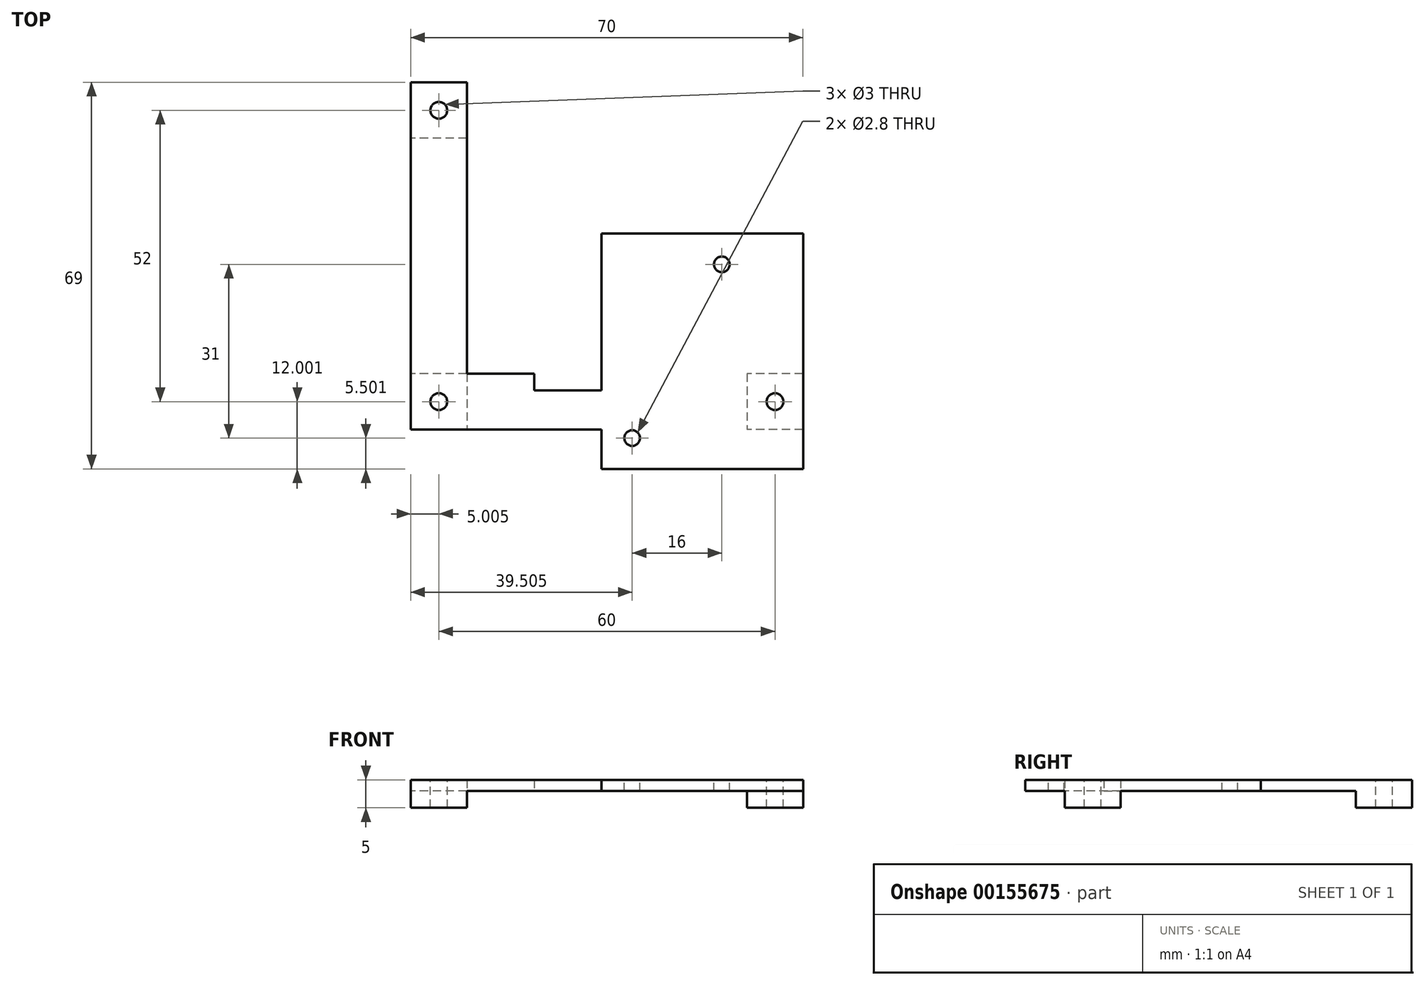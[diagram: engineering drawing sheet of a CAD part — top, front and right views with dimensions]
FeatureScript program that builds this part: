
annotation { "Feature Type Name" : "Feature", "Feature Type Description" : "" }
export const myFeature = defineFeature(function(context is Context, id is Id, definition is map)
    precondition{}
    {
        {
            var Q0;
            Q0=qCreatedBy(makeId("Top.planeOp"),FACE);
            var sketch = newSketch(context, id + "F0", { "sketchPlane" : qUnion([Q0])});
            skLineSegment(sketch, "E0", {"start": v(-62.44, 59.41) * mm, "end": v(-52.44, 59.41) * mm});
            skLineSegment(sketch, "E1", {"start": v(-52.44, 59.41) * mm, "end": v(-52.44, 7.41) * mm});
            skLineSegment(sketch, "E2", {"start": v(-52.44, 7.41) * mm, "end": v(-40.44, 7.41) * mm});
            skLineSegment(sketch, "E3", {"start": v(-40.44, 7.41) * mm, "end": v(-40.44, 4.41) * mm});
            skLineSegment(sketch, "E4", {"start": v(-40.44, 4.41) * mm, "end": v(-28.44, 4.41) * mm});
            skLineSegment(sketch, "E5", {"start": v(-28.44, 4.41) * mm, "end": v(-28.44, 32.41) * mm});
            skLineSegment(sketch, "E6", {"start": v(-28.44, 32.41) * mm, "end": v(7.56, 32.41) * mm});
            skLineSegment(sketch, "E7", {"start": v(7.56, 32.41) * mm, "end": v(7.56, -9.59) * mm});
            skLineSegment(sketch, "E8", {"start": v(7.56, -9.59) * mm, "end": v(-28.44, -9.59) * mm});
            skLineSegment(sketch, "E9", {"start": v(-28.44, -9.59) * mm, "end": v(-28.44, -2.59) * mm});
            skLineSegment(sketch, "E10", {"start": v(-28.44, -2.59) * mm, "end": v(-62.44, -2.59) * mm});
            skLineSegment(sketch, "E11", {"start": v(-62.44, -2.59) * mm, "end": v(-62.44, 59.41) * mm});
            skSolve(sketch);
        }
        {
            var Q0;
            Q0 = qSketchRegion(id + "F0", true);
            extrude(context, id + "F1", {"entities" : qUnion([Q0]), "depth" : 2 * mm});
        }
        {
            var Q0;
            Q0=makeQuery(id+"F1.opExtrude","CAP_FACE",FACE,{"disambiguationData":[OSD([sQuery(id+"F0.wireOp",EDGE,"E0"),sQuery(id+"F0.wireOp",EDGE,"E1"),sQuery(id+"F0.wireOp",EDGE,"E2"),sQuery(id+"F0.wireOp",EDGE,"E3"),sQuery(id+"F0.wireOp",EDGE,"E4"),sQuery(id+"F0.wireOp",EDGE,"E5"),sQuery(id+"F0.wireOp",EDGE,"E6"),sQuery(id+"F0.wireOp",EDGE,"E7"),sQuery(id+"F0.wireOp",EDGE,"E8"),sQuery(id+"F0.wireOp",EDGE,"E9"),sQuery(id+"F0.wireOp",EDGE,"E10"),sQuery(id+"F0.wireOp",EDGE,"E11")])],"isStart":true});
            var sketch = newSketch(context, id + "F2", { "sketchPlane" : qUnion([Q0])});
            skLineSegment(sketch, "E12.bottom", {"start": v(-52.44, -59.41) * mm, "end": v(-62.44, -59.41) * mm});
            skLineSegment(sketch, "E12.top", {"start": v(-52.44, -49.41) * mm, "end": v(-62.44, -49.41) * mm});
            skLineSegment(sketch, "E12.left", {"start": v(-52.44, -59.41) * mm, "end": v(-52.44, -49.41) * mm});
            skLineSegment(sketch, "E12.right", {"start": v(-62.44, -59.41) * mm, "end": v(-62.44, -49.41) * mm});
            skPoint(sketch, "E12.middle", {"position": v(-57.44, -54.41) * mm});
            skLineSegment(sketch, "E13.bottom", {"start": v(-52.44, -7.41) * mm, "end": v(-62.44, -7.41) * mm});
            skLineSegment(sketch, "E13.top", {"start": v(-52.44, 2.59) * mm, "end": v(-62.44, 2.59) * mm});
            skLineSegment(sketch, "E13.left", {"start": v(-52.44, -7.41) * mm, "end": v(-52.44, 2.59) * mm});
            skLineSegment(sketch, "E13.right", {"start": v(-62.44, -7.41) * mm, "end": v(-62.44, 2.59) * mm});
            skPoint(sketch, "E13.middle", {"position": v(-57.44, -2.41) * mm});
            skLineSegment(sketch, "E14.bottom", {"start": v(7.56, -7.41) * mm, "end": v(-2.44, -7.41) * mm});
            skLineSegment(sketch, "E14.top", {"start": v(7.56, 2.59) * mm, "end": v(-2.44, 2.59) * mm});
            skLineSegment(sketch, "E14.left", {"start": v(7.56, -7.41) * mm, "end": v(7.56, 2.59) * mm});
            skLineSegment(sketch, "E14.right", {"start": v(-2.44, -7.41) * mm, "end": v(-2.44, 2.59) * mm});
            skPoint(sketch, "E14.middle", {"position": v(2.56, -2.41) * mm});
            skSolve(sketch);
        }
        {
            var Q0;
            Q0 = qSketchRegion(id + "F2", true);
            extrude(context, id + "F3", {"entities" : qUnion([Q0]), "operationType" : NewBodyOperationType.ADD, "depth" : 3 * mm});
        }
        {
            var Q0;
            Q0=makeQuery(id+"F1.opExtrude","CAP_FACE",FACE,{"disambiguationData":[OSD([sQuery(id+"F0.wireOp",EDGE,"E0"),sQuery(id+"F0.wireOp",EDGE,"E1"),sQuery(id+"F0.wireOp",EDGE,"E2"),sQuery(id+"F0.wireOp",EDGE,"E3"),sQuery(id+"F0.wireOp",EDGE,"E4"),sQuery(id+"F0.wireOp",EDGE,"E5"),sQuery(id+"F0.wireOp",EDGE,"E6"),sQuery(id+"F0.wireOp",EDGE,"E7"),sQuery(id+"F0.wireOp",EDGE,"E8"),sQuery(id+"F0.wireOp",EDGE,"E9"),sQuery(id+"F0.wireOp",EDGE,"E10"),sQuery(id+"F0.wireOp",EDGE,"E11")])],"isStart":false});
            var sketch = newSketch(context, id + "F4", { "sketchPlane" : qUnion([Q0])});
            skCircle(sketch, "E15", {"center": v(-57.44, 54.41) * mm, "radius": 1.5 * mm});
            skCircle(sketch, "E16", {"center": v(-57.44, 2.41) * mm, "radius": 1.5 * mm});
            skCircle(sketch, "E17", {"center": v(2.56, 2.41) * mm, "radius": 1.5 * mm});
            skCircle(sketch, "E18", {"center": v(-6.94, 26.91) * mm, "radius": 1.4 * mm});
            skCircle(sketch, "E19", {"center": v(-22.94, -4.09) * mm, "radius": 1.4 * mm});
            skSolve(sketch);
        }
        {
            var Q0;
            Q0 = qSketchRegion(id + "F4", true);
            extrude(context, id + "F5", {"entities" : qUnion([Q0]), "operationType" : NewBodyOperationType.REMOVE, "oppositeDirection" : true, "depth" : 5 * mm});
        }
    });
